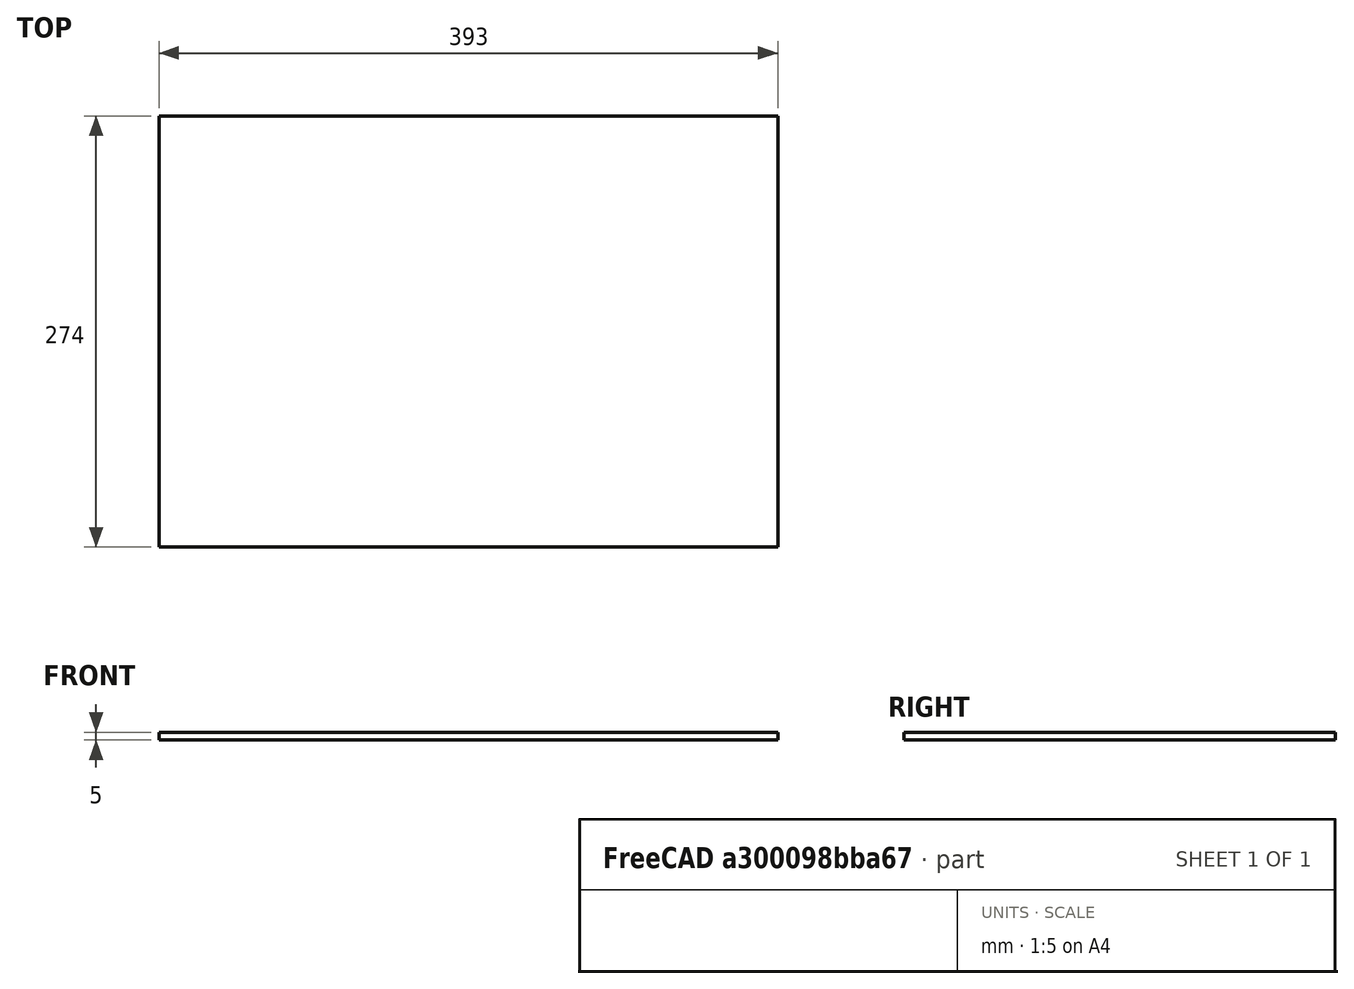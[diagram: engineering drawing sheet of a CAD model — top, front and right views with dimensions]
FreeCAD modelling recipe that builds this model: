
FCSTD DOCUMENT  (FreeCAD 0.19R24366 (Git))
Label: sailface
License: All rights reserved
LicenseURL: http://en.wikipedia.org/wiki/All_rights_reserved
objects: Sketcher::SketchObject×2, PartDesign::Pad×1, PartDesign::Body×1
note: 5 computed .brp shape members not serialized (recipe doc carries the construction recipe); baked Part::Feature solids carry a one-line shape summary decoded from their .brp

FEATURE [Sketcher::SketchObject] Sketch
  FullyConstrained = true
  MapMode = 5
  Support = -> [XY_Plane]
  sketch-geometry (4):
    g0: LineSegment StartX=0 StartY=0 StartZ=0 EndX=393 EndY=0 EndZ=0
    g1: LineSegment StartX=393 StartY=0 StartZ=0 EndX=393 EndY=274 EndZ=0
    g2: LineSegment StartX=393 StartY=274 StartZ=0 EndX=0 EndY=274 EndZ=0
    g3: LineSegment StartX=0 StartY=274 StartZ=0 EndX=0 EndY=0 EndZ=0
  constraints (11):
    c: Coincident(g0,g1)
    c: Coincident(g1,g2)
    c: Coincident(g2,g3)
    c: Coincident(g3,g0)
    c: Horizontal(g0)
    c: Horizontal(g2)
    c: Vertical(g1)
    c: Vertical(g3)
    c: Coincident(g0,g-1)
    c: DistanceX(g2,g2) = 393
    c: DistanceY(g3,g3) = 274
FEATURE [PartDesign::Pad] Pad  label="solarpanel"
  Direction = (1,1,1)
  Length = 5
  Length2 = 100
  Profile = -> Sketch
  Type = 0
FEATURE [Sketcher::SketchObject] Sketch001
  ExternalGeometry = -> [Pad]
  FullyConstrained = false
  MapMode = 5
  Placement = pos=(0,0,5) rot=(0,0,1;0rad)
  Support = -> [Pad]
  sketch-geometry (4):
    g0: LineSegment StartX=-20 StartY=284 StartZ=0 EndX=590 EndY=284 EndZ=0
    g1: LineSegment StartX=590 StartY=284 StartZ=0 EndX=590 EndY=-10 EndZ=0
    g2: LineSegment StartX=590 StartY=-10 StartZ=0 EndX=-20 EndY=-10 EndZ=0
    g3: LineSegment StartX=-20 StartY=-10 StartZ=0 EndX=-20 EndY=284 EndZ=0
  constraints (12):
    c: Coincident(g0,g1)
    c: Coincident(g1,g2)
    c: Coincident(g2,g3)
    c: Coincident(g3,g0)
    c: Horizontal(g0)
    c: Horizontal(g2)
    c: Vertical(g1)
    c: Vertical(g3)
    c: DistanceY(g-3,g0) = 10
    c: DistanceY(g2,g-1) = 10
    c: DistanceX(g0,g0) = 610
    c: DistanceX(g-3,g0) = -20
FEATURE [PartDesign::Body] Body
  Group = -> [Sketch,Pad,Sketch001]
  Origin = -> Origin
  Tip = -> Pad
